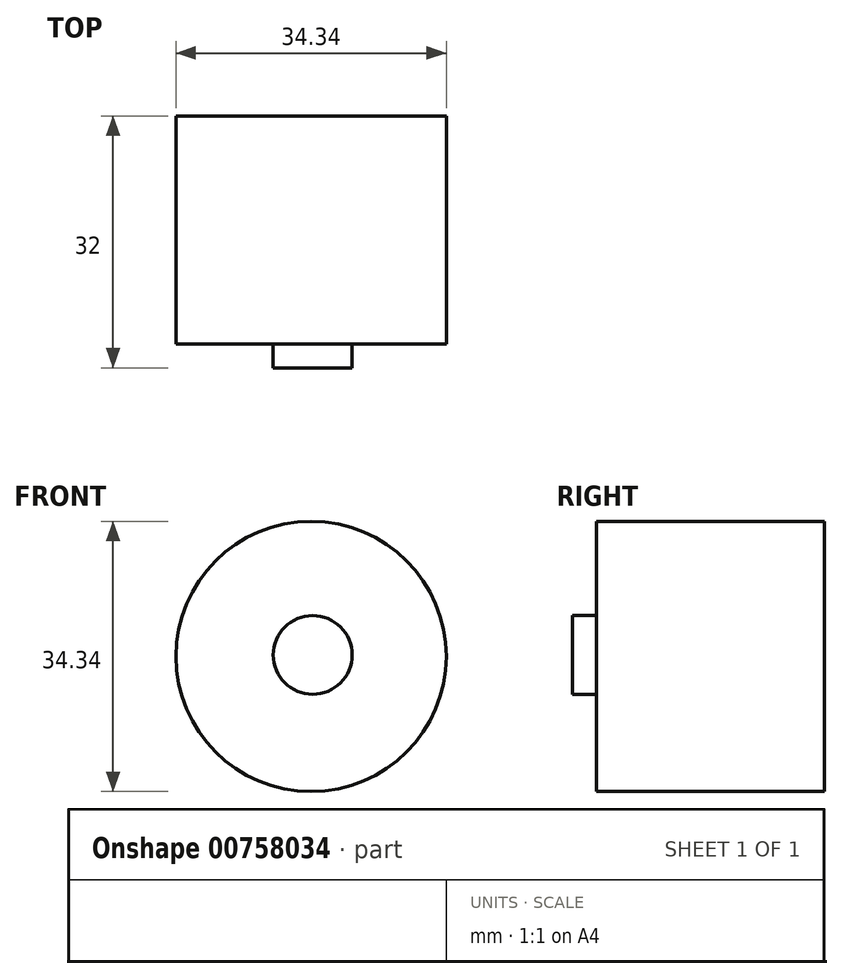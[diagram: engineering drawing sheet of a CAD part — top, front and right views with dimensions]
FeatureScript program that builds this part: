
annotation { "Feature Type Name" : "Feature", "Feature Type Description" : "" }
export const myFeature = defineFeature(function(context is Context, id is Id, definition is map)
    precondition{}
    {
        {
            var Q0;
            Q0=qCreatedBy(makeId("Front.planeOp"),FACE);
            var sketch = newSketch(context, id + "F0", { "sketchPlane" : qUnion([Q0])});
            skLineSegment(sketch, "E0.bottom", {"start": v(-17.14, 32.51) * mm, "end": v(23.01, 32.51) * mm});
            skLineSegment(sketch, "E0.top", {"start": v(-17.14, -20.37) * mm, "end": v(23.01, -20.37) * mm});
            skLineSegment(sketch, "E0.left", {"start": v(-17.14, 32.51) * mm, "end": v(-17.14, -20.37) * mm});
            skLineSegment(sketch, "E0.right", {"start": v(23.01, 32.51) * mm, "end": v(23.01, -20.37) * mm});
            skSolve(sketch);
        }
        {
            var Q0;
            Q0=makeQuery(id+"F0.imprint","IMPRINT",FACE,{"disambiguationData":[TD([[makeQuery(id+"F0.imprint","IMPRINT",EDGE,{"derivedFrom":sQuery(id+"F0.wireOp",EDGE,"E0.bottom")}),-1.0]])]});
            var Q1;
            Q1=sQuery(id+"F0.wireOp",EDGE,"E0.bottom");
            var Q2;
            Q2=sQuery(id+"F0.wireOp",EDGE,"E0.right");
            var Q3;
            Q3=sQuery(id+"F0.wireOp",EDGE,"E0.top");
            var Q4;
            Q4=sQuery(id+"F0.wireOp",EDGE,"E0.left");
            extrude(context, id + "F1", {"entities" : qUnion([Q0]), "bodyType" : ToolBodyType.SURFACE, "surfaceEntities" : qUnion([Q1, Q2, Q3, Q4]), "depth" : 37.6 * mm, "offsetDistance" : 25.4 * mm});
        }
        {
            var Q0;
            Q0=makeQuery(id+"F1.opExtrude","SWEPT_EDGE",EDGE,{"disambiguationData":[OSD([sQuery(id+"F0.wireOp",VERTEX,"E0.right.start")])]});
            fillet(context, id + "F2", {"entities" : qUnion([Q0]), "radius" : 52.12 * mm, "tangentPropagation" : true, "allowEdgeOverflow" : false});
        }
        {
            var Q0;
            Q0=makeQuery(id+"F1.opExtrude","SWEPT_EDGE",EDGE,{"disambiguationData":[OSD([sQuery(id+"F0.wireOp",VERTEX,"E0.left.end")])]});
            fillet(context, id + "F3", {"entities" : qUnion([Q0]), "radius" : 38.63 * mm, "tangentPropagation" : true, "allowEdgeOverflow" : false});
        }
        {
            var Q0;
            Q0=qCreatedBy(makeId("Front.planeOp"),FACE);
            var sketch = newSketch(context, id + "F4", { "sketchPlane" : qUnion([Q0])});
            skCircle(sketch, "E1", {"center": v(2.45, 4.9) * mm, "radius": 17.17 * mm});
            skSolve(sketch);
        }
        {
            var Q0;
            Q0=makeQuery(id+"F4.imprint","IMPRINT",FACE,{"disambiguationData":[TD([[makeQuery(id+"F4.imprint","IMPRINT",EDGE,{"derivedFrom":sQuery(id+"F4.wireOp",EDGE,"E1")}),1.0]])]});
            var Q1;
            Q1=sQuery(id+"F4.wireOp",EDGE,"E1");
            extrude(context, id + "F5", {"entities" : qUnion([Q0]), "surfaceEntities" : qUnion([Q1]), "depth" : 28.96 * mm, "offsetDistance" : 25.4 * mm});
        }
        {
            var Q0;
            Q0=qCreatedBy(makeId("Front.planeOp"),FACE);
            var sketch = newSketch(context, id + "F6", { "sketchPlane" : qUnion([Q0])});
            skCircle(sketch, "E2", {"center": v(2.64, 5.1) * mm, "radius": 5 * mm});
            skSolve(sketch);
        }
        {
            var Q0;
            Q0=makeQuery(id+"F6.imprint","IMPRINT",FACE,{"disambiguationData":[TD([[makeQuery(id+"F6.imprint","IMPRINT",EDGE,{"derivedFrom":sQuery(id+"F6.wireOp",EDGE,"E2")}),1.0]])]});
            var Q1;
            Q1=sQuery(id+"F6.wireOp",EDGE,"E2");
            extrude(context, id + "F7", {"entities" : qUnion([Q0]), "operationType" : NewBodyOperationType.ADD, "surfaceEntities" : qUnion([Q1]), "depth" : 32 * mm, "offsetDistance" : 25.4 * mm});
        }
    });
